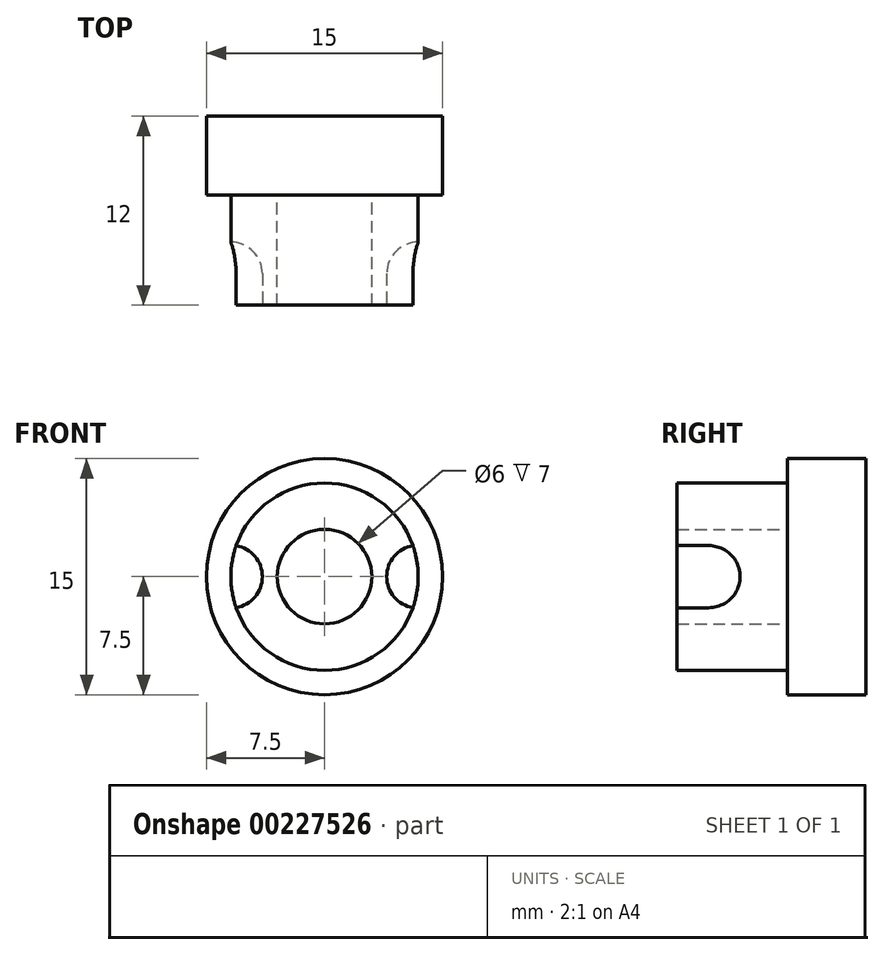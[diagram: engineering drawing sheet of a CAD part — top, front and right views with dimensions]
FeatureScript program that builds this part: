
annotation { "Feature Type Name" : "Feature", "Feature Type Description" : "" }
export const myFeature = defineFeature(function(context is Context, id is Id, definition is map)
    precondition{}
    {
        {
            var Q0;
            Q0=qCreatedBy(makeId("Front.planeOp"),FACE);
            var sketch = newSketch(context, id + "F0", { "sketchPlane" : qUnion([Q0])});
            skCircle(sketch, "E0", {"center": v(0, 0) * mm, "radius": 7.5 * mm});
            skSolve(sketch);
        }
        {
            var Q0;
            Q0=qSketchRegion(id+"F0",true);
            extrude(context, id + "F1", {"entities" : qUnion([Q0]), "oppositeDirection" : true, "depth" : 5 * mm});
        }
        {
            var Q0;
            Q0=makeQuery(id+"F1.opExtrude","CAP_FACE",FACE,{"disambiguationData":[OSD([sQuery(id+"F0.wireOp",EDGE,"E0")])],"isStart":false});
            var sketch = newSketch(context, id + "F2", { "sketchPlane" : qUnion([Q0])});
            skCircle(sketch, "E1", {"center": v(0, 0) * mm, "radius": 5.95 * mm});
            skCircle(sketch, "E2", {"center": v(0, 0) * mm, "radius": 3 * mm});
            skSolve(sketch);
        }
        {
            var Q0;
            Q0=qSketchRegion(id+"F2",true);
            extrude(context, id + "F3", {"entities" : qUnion([Q0]), "operationType" : NewBodyOperationType.ADD, "oppositeDirection" : true, "depth" : 12 * mm});
        }
        {
            var Q0;
            Q0=makeQuery(id+"F3.opExtrude","CAP_FACE",FACE,{"disambiguationData":[OSD([sQuery(id+"F2.wireOp",EDGE,"E1"),sQuery(id+"F2.wireOp",EDGE,"E2")])],"isStart":false});
            var sketch = newSketch(context, id + "F4", { "sketchPlane" : qUnion([Q0])});
            skArc(sketch, "E3", {"start": v(-5.61, -1.97) * mm, "mid": v(-3.95, 0) * mm, "end": v(-5.61, 1.97) * mm});
            skArc(sketch, "E4", {"start": v(5.61, 1.97) * mm, "mid": v(3.95, 0) * mm, "end": v(5.61, -1.97) * mm});
            skArc(sketch, "E5", {"start": v(-5.61, 1.97) * mm, "mid": v(-5.95, 0) * mm, "end": v(-5.61, -1.97) * mm});
            skArc(sketch, "E6.trimOffspring", {"start": v(5.61, -1.97) * mm, "mid": v(5.95, 0) * mm, "end": v(5.61, 1.97) * mm});
            skSolve(sketch);
        }
        {
            var Q0;
            Q0 = qSketchRegion(id + "F4", true);
            extrude(context, id + "F5", {"entities" : qUnion([Q0]), "operationType" : NewBodyOperationType.REMOVE, "oppositeDirection" : true, "depth" : 4 * mm});
        }
        {
            var Q0;
            Q0=makeQuery(id+"F5.boolean.opBoolean","COPY",EDGE,{"derivedFrom":makeQuery(id+"F5.opExtrude","CAP_EDGE",EDGE,{"disambiguationData":[OSD([sQuery(id+"F4.wireOp",EDGE,"E3")])],"isStart":false})});
            var Q1;
            Q1=makeQuery(id+"F5.boolean.opBoolean","COPY",EDGE,{"derivedFrom":makeQuery(id+"F5.opExtrude","CAP_EDGE",EDGE,{"disambiguationData":[OSD([sQuery(id+"F4.wireOp",EDGE,"E4")])],"isStart":false})});
            fillet(context, id + "F6", {"entities" : qUnion([Q0, Q1]), "radius" : 2 * mm, "tangentPropagation" : true, "allowEdgeOverflow" : false});
        }
    });
